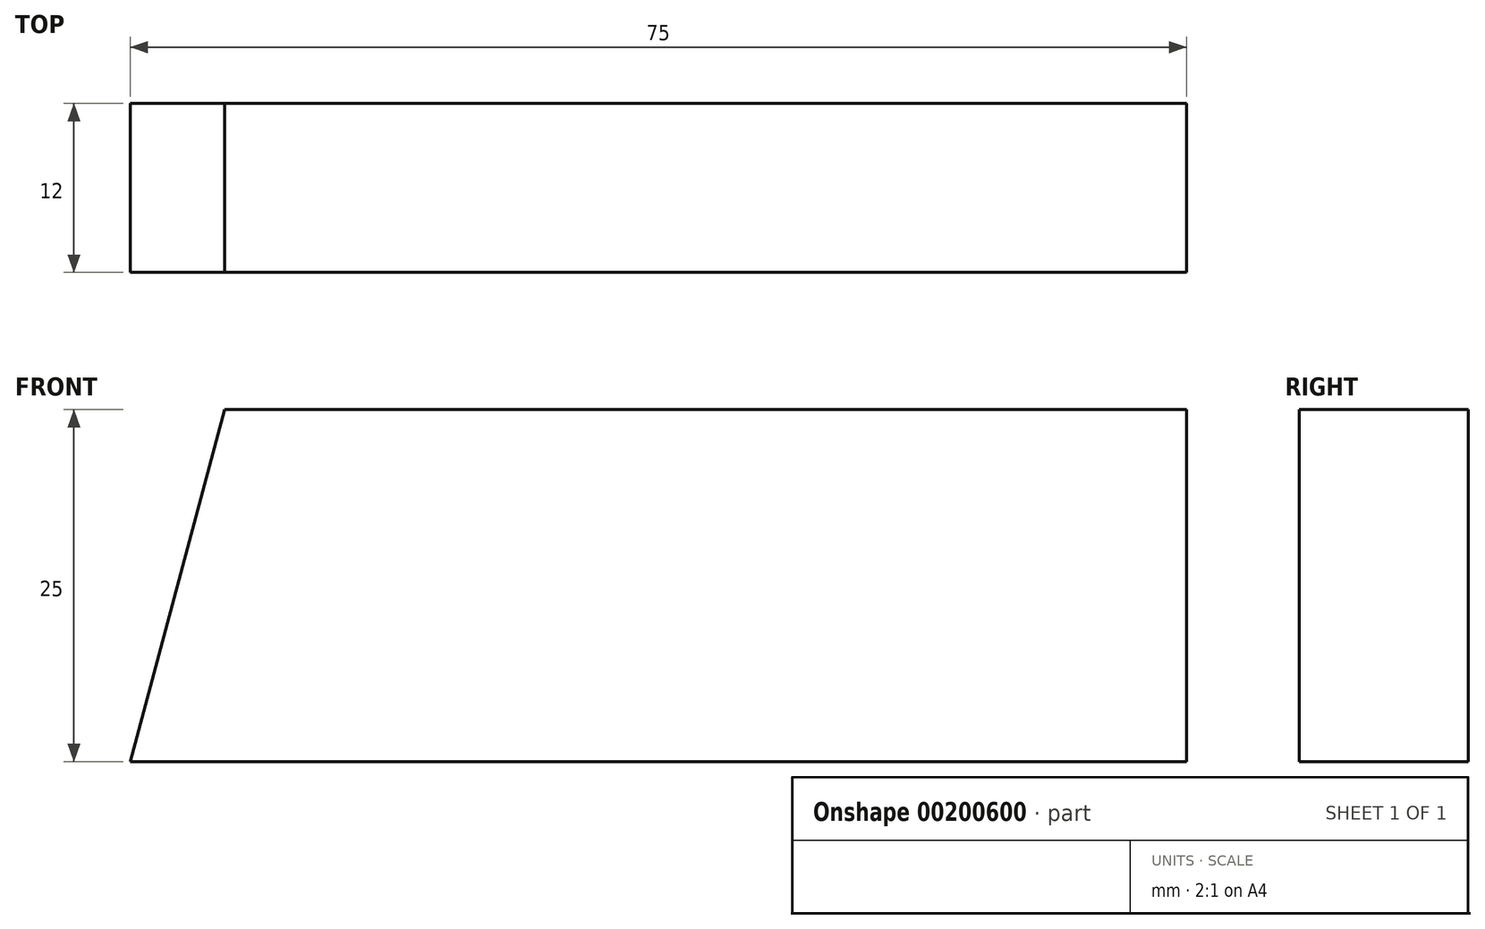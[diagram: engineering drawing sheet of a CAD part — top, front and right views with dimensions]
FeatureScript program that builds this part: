
annotation { "Feature Type Name" : "Feature", "Feature Type Description" : "" }
export const myFeature = defineFeature(function(context is Context, id is Id, definition is map)
    precondition{}
    {
        {
            var Q0;
            Q0=qCreatedBy(makeId("Front.planeOp"),FACE);
            var sketch = newSketch(context, id + "F0", { "sketchPlane" : qUnion([Q0])});
            skLineSegment(sketch, "E0", {"start": v(0, 0) * mm, "end": v(0, 25) * mm});
            skLineSegment(sketch, "E1", {"start": v(0, 25) * mm, "end": v(-68.3, 25) * mm});
            skLineSegment(sketch, "E2", {"start": v(-68.3, 25) * mm, "end": v(-75, 0) * mm});
            skLineSegment(sketch, "E3", {"start": v(-75, 0) * mm, "end": v(0, 0) * mm});
            skSolve(sketch);
        }
        {
            var Q0;
            Q0 = qSketchRegion(id + "F0", true);
            extrude(context, id + "F1", {"entities" : qUnion([Q0]), "depth" : 12 * mm});
        }
    });
